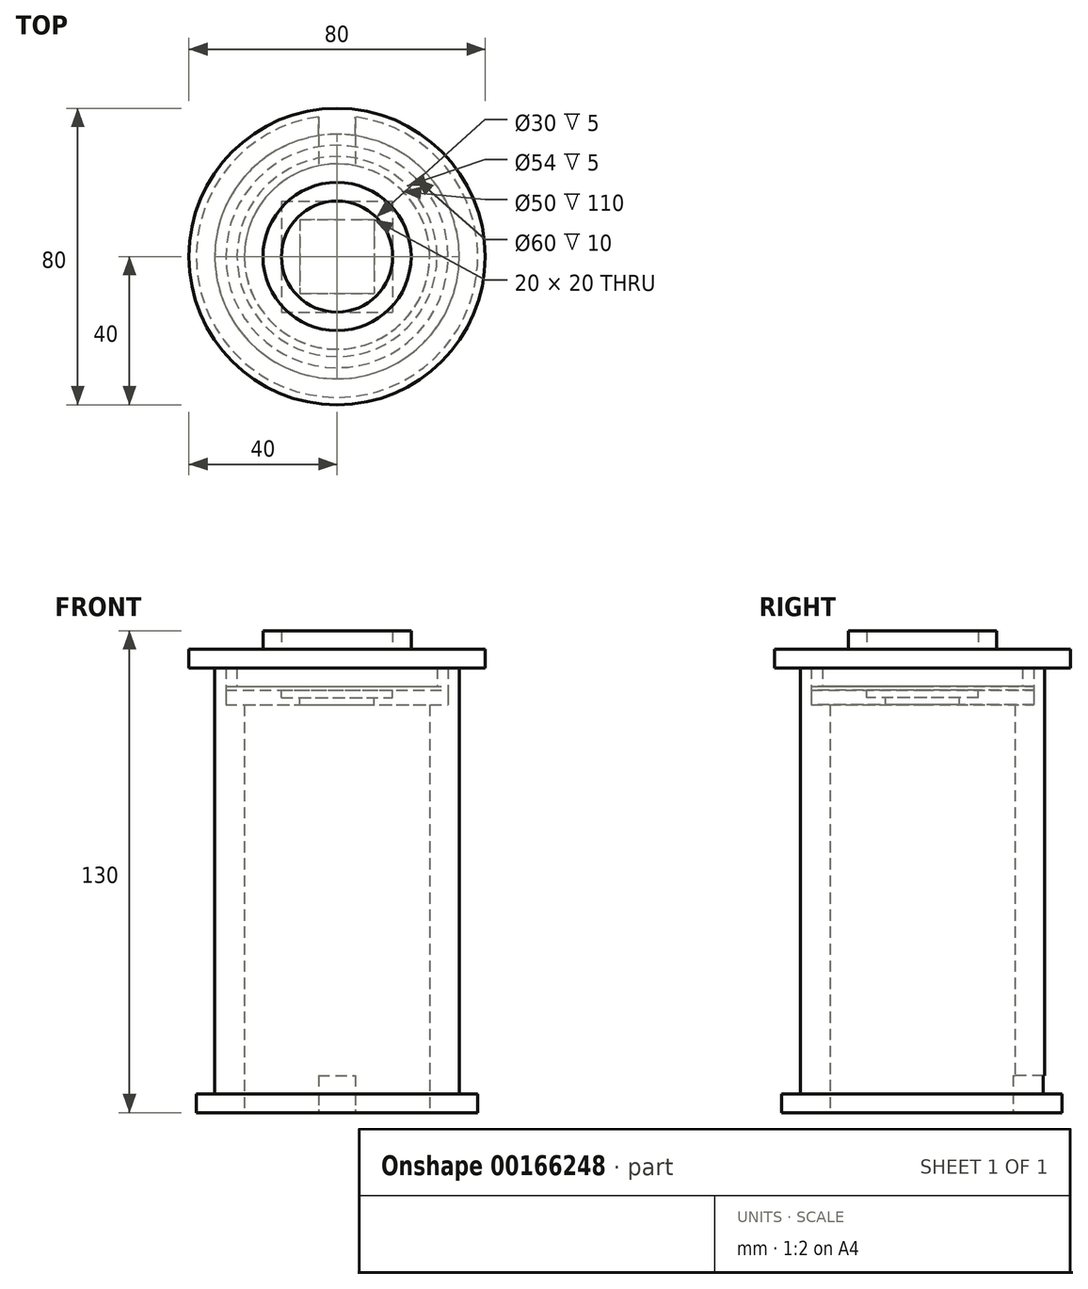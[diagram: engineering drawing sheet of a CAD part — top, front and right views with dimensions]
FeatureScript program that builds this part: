
annotation { "Feature Type Name" : "Feature", "Feature Type Description" : "" }
export const myFeature = defineFeature(function(context is Context, id is Id, definition is map)
    precondition{}
    {
        {
            var Q0;
            Q0=qCreatedBy(makeId("Front.planeOp"),FACE);
            var sketch = newSketch(context, id + "F0", { "sketchPlane" : qUnion([Q0])});
            skLineSegment(sketch, "E0.top", {"start": v(40, 120) * mm, "end": v(30, 120) * mm});
            skLineSegment(sketch, "E1.top", {"start": v(27, 115) * mm, "end": v(30, 115) * mm});
            skLineSegment(sketch, "E2", {"start": v(40, 120) * mm, "end": v(40, 125) * mm});
            skLineSegment(sketch, "E3", {"start": v(40, 125) * mm, "end": v(20, 125) * mm});
            skLineSegment(sketch, "E4", {"start": v(20, 125) * mm, "end": v(20, 130) * mm});
            skLineSegment(sketch, "E5", {"start": v(20, 130) * mm, "end": v(15, 130) * mm});
            skLineSegment(sketch, "E6", {"start": v(15, 130) * mm, "end": v(15, 125) * mm});
            skLineSegment(sketch, "E7", {"start": v(15, 125) * mm, "end": v(0, 125) * mm});
            skLineSegment(sketch, "E8", {"start": v(0, 125) * mm, "end": v(0, 120) * mm});
            skLineSegment(sketch, "E9", {"start": v(30, 115) * mm, "end": v(30, 115) * mm});
            skLineSegment(sketch, "E10", {"start": v(0, 120) * mm, "end": v(27, 120) * mm});
            skLineSegment(sketch, "E11", {"start": v(30, 115) * mm, "end": v(30, 120) * mm});
            skLineSegment(sketch, "E12", {"start": v(27, 120) * mm, "end": v(27, 115) * mm});
            skPoint(sketch, "E13.orphan", {"position": v(30, 120) * mm});
            skLineSegment(sketch, "E14", {"start": v(25, 110) * mm, "end": v(25, 0) * mm});
            skLineSegment(sketch, "E15", {"start": v(0, 0) * mm, "end": v(0, 114) * mm, "construction": true});
            skLineSegment(sketch, "E16.trimOffspring", {"start": v(0, 120) * mm, "end": v(0, 125) * mm, "construction": true});
            skLineSegment(sketch, "E17.top", {"start": v(30, 110) * mm, "end": v(0, 110) * mm});
            skLineSegment(sketch, "E17.left", {"start": v(30, 115) * mm, "end": v(30, 110) * mm});
            skLineSegment(sketch, "E17.right", {"start": v(0, 114) * mm, "end": v(0, 110) * mm});
            skLineSegment(sketch, "E18", {"start": v(0, 114) * mm, "end": v(30, 114) * mm});
            skLineSegment(sketch, "E19", {"start": v(25, 0) * mm, "end": v(38, 0) * mm});
            skLineSegment(sketch, "E20", {"start": v(38, 0) * mm, "end": v(38, 5) * mm});
            skLineSegment(sketch, "E21", {"start": v(38, 5) * mm, "end": v(33, 5) * mm});
            skLineSegment(sketch, "E22", {"start": v(33, 5) * mm, "end": v(33, 120) * mm});
            skLineSegment(sketch, "E23", {"start": v(33, 120) * mm, "end": v(30, 120) * mm});
            skLineSegment(sketch, "E24", {"start": v(30, 120) * mm, "end": v(30, 110) * mm});
            skLineSegment(sketch, "E25", {"start": v(30, 110) * mm, "end": v(25, 110) * mm});
            skSolve(sketch);
        }
        {
            var Q0;
            Q0=makeQuery(id+"F0.imprint","IMPRINT",FACE,{"disambiguationData":[TD([[makeQuery(id+"F0.imprint","IMPRINT",EDGE,{"derivedFrom":sQuery(id+"F0.wireOp",EDGE,"E14")}),1.0]])]});
            var Q1;
            Q1=sQuery(id+"F0.wireOp",EDGE,"E15");
            revolve(context, id + "F1", {"entities" : qUnion([Q0]), "axis" : qUnion([Q1]), "revolveType" : RevolveType.FULL});
        }
        {
            var Q0;
            Q0=makeQuery(id+"F0.imprint","IMPRINT",FACE,{"disambiguationData":[TD([[makeQuery(id+"F0.imprint","IMPRINT",EDGE,{"derivedFrom":sQuery(id+"F0.wireOp",EDGE,"E0.top")}),-1.0]])]});
            var Q1;
            Q1=sQuery(id+"F0.wireOp",EDGE,"E15");
            revolve(context, id + "F2", {"entities" : qUnion([Q0]), "axis" : qUnion([Q1]), "revolveType" : RevolveType.FULL});
        }
        {
            var Q0;
            Q0=makeQuery(id+"F0.imprint","IMPRINT",FACE,{"disambiguationData":[TD([[makeQuery(id+"F0.imprint","IMPRINT",EDGE,{"derivedFrom":sQuery(id+"F0.wireOp",EDGE,"E17.top")}),-1.0]])]});
            var Q1;
            Q1=sQuery(id+"F0.wireOp",EDGE,"E15");
            revolve(context, id + "F3", {"entities" : qUnion([Q0]), "axis" : qUnion([Q1]), "revolveType" : RevolveType.FULL});
        }
        {
            var Q0;
            Q0=qCreatedBy(makeId("Front.planeOp"),FACE);
            var sketch = newSketch(context, id + "F4", { "sketchPlane" : qUnion([Q0])});
            skLineSegment(sketch, "E26.bottom", {"start": v(-5, 0) * mm, "end": v(5, 0) * mm});
            skLineSegment(sketch, "E26.top", {"start": v(-5, 10) * mm, "end": v(5, 10) * mm});
            skLineSegment(sketch, "E26.left", {"start": v(-5, 0) * mm, "end": v(-5, 10) * mm});
            skLineSegment(sketch, "E26.right", {"start": v(5, 0) * mm, "end": v(5, 10) * mm});
            skSolve(sketch);
        }
        {
            var Q0;
            Q0 = qSketchRegion(id + "F4", true);
            extrude(context, id + "F5", {"entities" : qUnion([Q0]), "operationType" : NewBodyOperationType.REMOVE, "oppositeDirection" : true, "depth" : 77.6 * mm});
        }
        {
            var Q0;
            Q0=makeQuery(id+"F3.opRevolve","SWEPT_FACE",FACE,{"disambiguationData":[OSD([sQuery(id+"F0.wireOp",EDGE,"E18")])]});
            var sketch = newSketch(context, id + "F6", { "sketchPlane" : qUnion([Q0])});
            skLineSegment(sketch, "E27.bottom", {"start": v(-15, 15) * mm, "end": v(15, 15) * mm});
            skLineSegment(sketch, "E27.top", {"start": v(-15, -15) * mm, "end": v(15, -15) * mm});
            skLineSegment(sketch, "E27.left", {"start": v(-15, 15) * mm, "end": v(-15, -15) * mm});
            skLineSegment(sketch, "E27.right", {"start": v(15, 15) * mm, "end": v(15, -15) * mm});
            skLineSegment(sketch, "E28", {"start": v(-15, 15) * mm, "end": v(15, -15) * mm, "construction": true});
            skLineSegment(sketch, "E29", {"start": v(-15, -15) * mm, "end": v(15, 15) * mm, "construction": true});
            skSolve(sketch);
        }
        {
            var Q0;
            Q0 = qSketchRegion(id + "F6", true);
            extrude(context, id + "F7", {"entities" : qUnion([Q0]), "operationType" : NewBodyOperationType.REMOVE, "oppositeDirection" : true, "depth" : 2 * mm});
        }
        {
            var Q0;
            Q0=makeQuery(id+"F7.boolean.opBoolean","COPY",FACE,{"derivedFrom":makeQuery(id+"F7.opExtrude","CAP_FACE",FACE,{"disambiguationData":[OSD([sQuery(id+"F6.wireOp",EDGE,"E27.bottom"),sQuery(id+"F6.wireOp",EDGE,"E27.top"),sQuery(id+"F6.wireOp",EDGE,"E27.left"),sQuery(id+"F6.wireOp",EDGE,"E27.right")])],"isStart":false})});
            var sketch = newSketch(context, id + "F8", { "sketchPlane" : qUnion([Q0])});
            skLineSegment(sketch, "E30.bottom", {"start": v(-10, 10) * mm, "end": v(10, 10) * mm});
            skLineSegment(sketch, "E30.top", {"start": v(-10, -10) * mm, "end": v(10, -10) * mm});
            skLineSegment(sketch, "E30.left", {"start": v(-10, 10) * mm, "end": v(-10, -10) * mm});
            skLineSegment(sketch, "E30.right", {"start": v(10, 10) * mm, "end": v(10, -10) * mm});
            skLineSegment(sketch, "E31", {"start": v(-10, 10) * mm, "end": v(10, -10) * mm, "construction": true});
            skLineSegment(sketch, "E32", {"start": v(10, 10) * mm, "end": v(-10, -10) * mm, "construction": true});
            skSolve(sketch);
        }
        {
            var Q0;
            Q0 = qSketchRegion(id + "F8", true);
            extrude(context, id + "F9", {"entities" : qUnion([Q0]), "operationType" : NewBodyOperationType.REMOVE, "oppositeDirection" : true, "depth" : 2 * mm});
        }
    });
